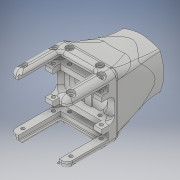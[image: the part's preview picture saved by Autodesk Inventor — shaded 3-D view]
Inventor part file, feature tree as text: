
AUTODESK INVENTOR PART (.ipt)
format: ipt  version: 2019 (Build 230136000, 136)  size: 1,632,768 bytes
history: native  units: mm
features: extrude x13, sketch x11, fillet x7, mirror x6, plane x4, chamfer x2, projected_geometry x2, loft x1
ambient origin geometry x8: Origin, YZ Plane, XZ Plane, XY Plane, X Axis, Y Axis, Z Axis, Center Point
bodies: Solid1 (feature_tree)
feature tree (46):
  plane  "Work Plane1"
  sketch  "Sketch2"  dims[d2=38.0mm d3=29.5mm]
  extrude  "Extrusion1"  Depth=29.5mm
  extrude  "Extrusion2"  Depth=25.0mm
  extrude  "Extrusion3"  Depth=36.0mm TaperAngle=0.0deg
  mirror  "Mirror2"
  sketch  "Sketch5"  dims[d10=17.25mm d11=5.6mm d12=2.0mm]
  mirror  "Mirror1"
  fillet  "Fillet1"  Radius=5.6mm
  extrude  "Extrusion4"  Depth=5.6mm
  fillet  "Fillet2"  Radius=2.0mm
  extrude  "Extrusion5"  Depth=4.0mm
  extrude  "Extrusion9"  Depth=5.0mm
  extrude  "Extrusion10"  Depth=5.6mm TaperAngle=0.0deg
  chamfer  "Chamfer2"  Distance=5.6mm
  mirror  "Mirror3"
  extrude  "Extrusion6"  Depth=34.6mm
  extrude  "Extrusion7"  Depth=2.7mm
  mirror  "Mirror4"
  mirror  "Mirror5"
  extrude  "Extrusion8"  Depth=22.0mm
  fillet  "Fillet3"  Radius=30.1mm
  plane  "Work Plane2"
  extrude  "Extrusion11"  Depth=2.5mm
  sketch  "Sketch9"  dims[d28=9.773844mm d32=5.6mm d33=0.0mm]
  sketch  "Sketch10"  dims[d34=3.75mm]
  plane  "Work Plane9"
  loft  "Loft7"
  mirror  "Mirror14"
  fillet  "Fillet13"  Radius=2.5mm
  fillet  "Fillet14"  Radius=5.0mm
  plane  "Work Plane10"
  extrude  "Extrusion13"  Depth=2.5mm
  chamfer  "Chamfer5"  Distance=5.0mm
  sketch  "Sketch17"  dims[d39=8.1mm d40=34.6mm d41=2.7mm d42=22.0mm d43=30.1mm d44=2.5mm d45=5.0mm d46=2.5mm d47=5.0mm d48=2.5mm d49=5.0mm d50=10.0mm d51=0.0mm d52=2.0mm d53=0.0mm d60=2.0mm d61=2.0mm d62=2.0mm d63=0.0mm d64=4.0mm d65=0.5mm d71=11.0mm d72=0.0mm d73=4.0mm d74=4.0mm d75=3.0mm d76=0.0mm d80=1.0mm d81=2.0mm d82=45.0deg d83=2.0mm d84=2.0mm d85=2.0mm d86=5.0mm d87=1.5mm d88=10.0mm d89=0.0mm d133=32.0mm d134=0.0mm d135=90.0deg d136=0.0mm d137=90.0deg d138=4.0mm d139=60.0mm d140=0.0mm d141=24.0mm d142=10.0mm d143=0.0mm d144=2.0mm d145=2.0mm d146=45.0deg d149=40.7mm d150=40.7mm d157=70.0mm d158=4.0mm d159=10.0mm d160=0.0mm]
  fillet  "Fillet16"  Radius=10.0mm
  fillet  "Fillet17"  Radius=2.0mm
  extrude  "Extrusion17"  Depth=2.0mm
  sketch  "Sketch3"  dims[d4=41.5mm d5=25.0mm]
  sketch  "Sketch4"  dims[d6=29.5mm d7=36.0mm d8=0.0mm d9=5.6mm]
  sketch  "Sketch7"  dims[d13=5.6mm d14=0.0mm d15=4.0mm]
  projected_geometry  "Projected Loop1"
  sketch  "Sketch8"  dims[d17=5.6mm d18=0.0mm d27=5.0mm]
  projected_geometry  "Projected Loop2"
  sketch  "Sketch15"  dims[d35=0.5mm]
  sketch  "Sketch16"  dims[d36=4.0mm d37=5.6mm d38=0.0mm]
